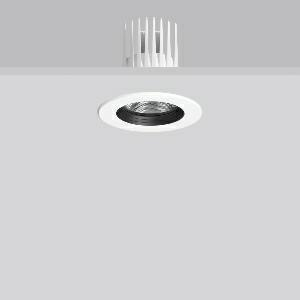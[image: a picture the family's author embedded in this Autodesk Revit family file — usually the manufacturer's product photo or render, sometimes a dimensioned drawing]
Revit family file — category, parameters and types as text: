
# Revit family: heledon_mini_e_901740_002_1_f5dd
name_source: partatom
category: Lighting Fixtures
units: mm (PartAtom-declared; Revit-internal decimal feet)

## family parameters
Cut with Voids When Loaded = No
Host = Face
Light Source = No
Part Type = Normal
Room Calculation Point = No
Round Connector Dimension = Use Diameter
Shared = No

## types (1)
- HELEDON mini E (1 x LED Modul 940, 2700 lm, 4000)
    Apparent Load = 20 VA
    Approval mark = CE
    CIE Flux Codes = 100 100 100 100 100
    Color Rendering = 92
    Color Temperature = 4000
    Default Elevation = 1800 mm
    Description = Series: HELEDON mini
Round recessed downlight. Housing: die-cast aluminium, powder-coated. Black plastic ring and recessed LED to prevent glare from the side. Optical assembly with reflector made of MIRO-Silver with 98% total light reflection for outstanding efficiency - can be changed without tools. Best colour rendering index Ra>90. Suitable for Recessed ceiling mounting. Installation without tools thanks to spring fastening system. Including separate LED converter with connecting cable 600 mm.High quality converter without flickering and stroboscopic effect. Through-wiring box (5 pole) available as accessory. The following accessories can be mounted without use of tools: interchangeable lenses, decorative glasses, honeycomb louvre, clear and frosted diffusers, white interchangeable plastic ring. 
Colour: traffic white, matt (RAL 9016)
Diameter: 124 mm
Height: 3 mm
Cut-out diameter: 114 mm
Recess height: 170 mm
Luminaire: recess height: 120 mm
Lamp: LED
Socket: without socket
Colour temperature: 4000K
Colour rendering index (CRI): 92
System power: 20 W
Rated luminous flux: 2700 lm
Luminous efficiency: 135 lm/W
Control gear: Regulated power supply
Protection class: II
Type of protection: IP 20
    Height = 0 mm  [stored 0 ft]
    Lamp = 1 x LED Modul 940
    Lamp Light Flux = 2700 lm
    Lamp count = 1
    Length = 124 mm  [stored 0.406824 ft]
    Lifetime = 50000 h
    Luminous efficacy = 135 lm/W
    Manufacturer = RZB
    ModVariant = No
    Model = 901740.002.1
    Mounting Place = Ceiling
    Mounting Type = Recessed
    Number of Poles = 1
    OnlyDefault = Yes
    Power Factor = 1
    Product Name = HELEDON mini E
    Product group = Recessed downlights
    ProductGroupID = 402
    Protection Class = Protection class II
    Protection Degree = IP 20
    RLX_Detail_Level = 1
    RLX_Emergency_Light_Flux = 0 lm
    RLX_Emergency_Type = 0
    RLX_Emergency_Type_DB = No
    RlxData = <blob elided: 128357 chars, md5=3ad662d3>
    Socket = socket
    Standby Power = 0 W
    System Light Flux = 2700 lm
    System Power = 20 W
    Type Comments = Product without accessories
    Type Image = 901657.002.jpg
    URL = http://relux.com
    VarID = ---
    Voltage = 230 V
    Voltage Range = 220-240 V
    Weight = 0.00 kg
    Width = 0 mm  [stored 0 ft]

note: [stored X ft] marks values corroborated as IEEE doubles in the binary element streams (Revit-internal decimal feet)

## geometry (parser evidence)
native form markers: Blend x4, Sweep x11
no freeform markers — native parametric forms only
